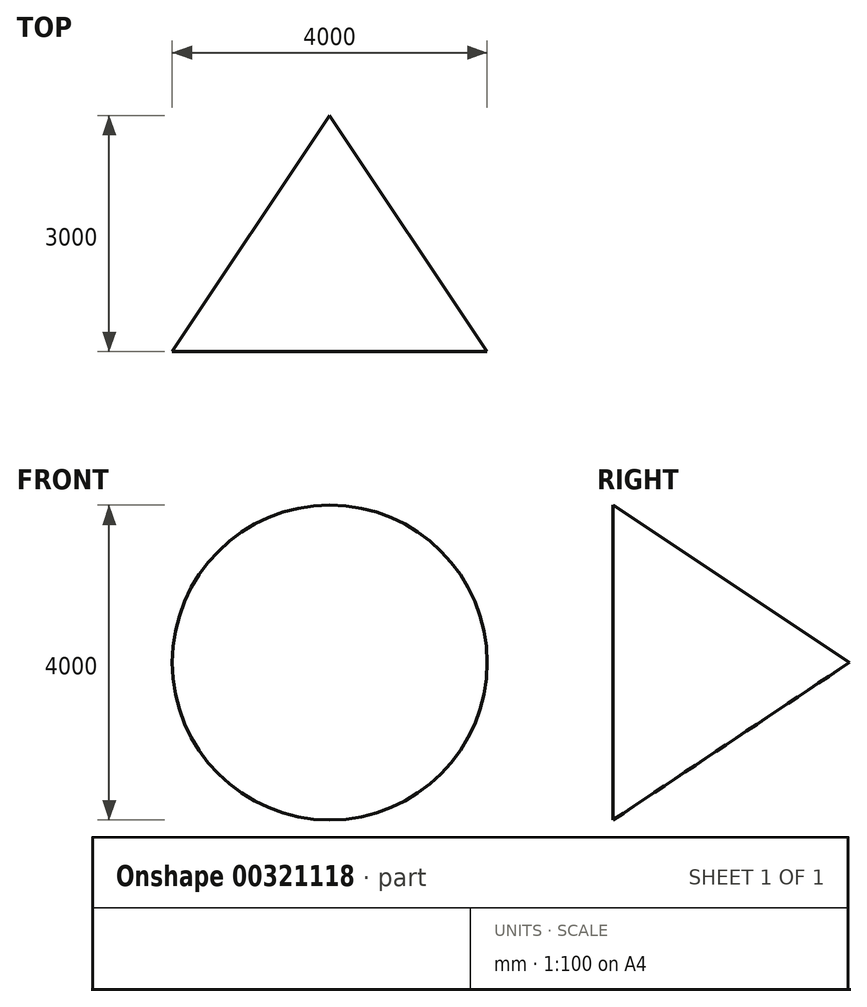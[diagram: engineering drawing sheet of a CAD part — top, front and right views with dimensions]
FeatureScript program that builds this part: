
annotation { "Feature Type Name" : "Feature", "Feature Type Description" : "" }
export const myFeature = defineFeature(function(context is Context, id is Id, definition is map)
    precondition{}
    {
        {
            var Q0;
            Q0=qCreatedBy(makeId("Top.planeOp"),FACE);
            var sketch = newSketch(context, id + "F0", { "sketchPlane" : qUnion([Q0])});
            skLineSegment(sketch, "E0", {"start": v(0, 0) * mm, "end": v(0, 3000) * mm});
            skLineSegment(sketch, "E1", {"start": v(0, 3000) * mm, "end": v(2000, 0) * mm});
            skLineSegment(sketch, "E2", {"start": v(2000, 0) * mm, "end": v(0, 0) * mm});
            skLineSegment(sketch, "E3", {"start": v(0, 4027.55) * mm, "end": v(0, -1629.02) * mm, "construction": true});
            skSolve(sketch);
        }
        {
            var Q0;
            Q0=makeQuery(id+"F0.imprint","IMPRINT",FACE,{"disambiguationData":[TD([[makeQuery(id+"F0.imprint","IMPRINT",EDGE,{"derivedFrom":sQuery(id+"F0.wireOp",EDGE,"E0")}),-1.0]])]});
            var Q1;
            Q1=sQuery(id+"F0.wireOp",EDGE,"E3");
            revolve(context, id + "F1", {"entities" : qUnion([Q0]), "axis" : qUnion([Q1]), "revolveType" : RevolveType.FULL});
        }
    });
